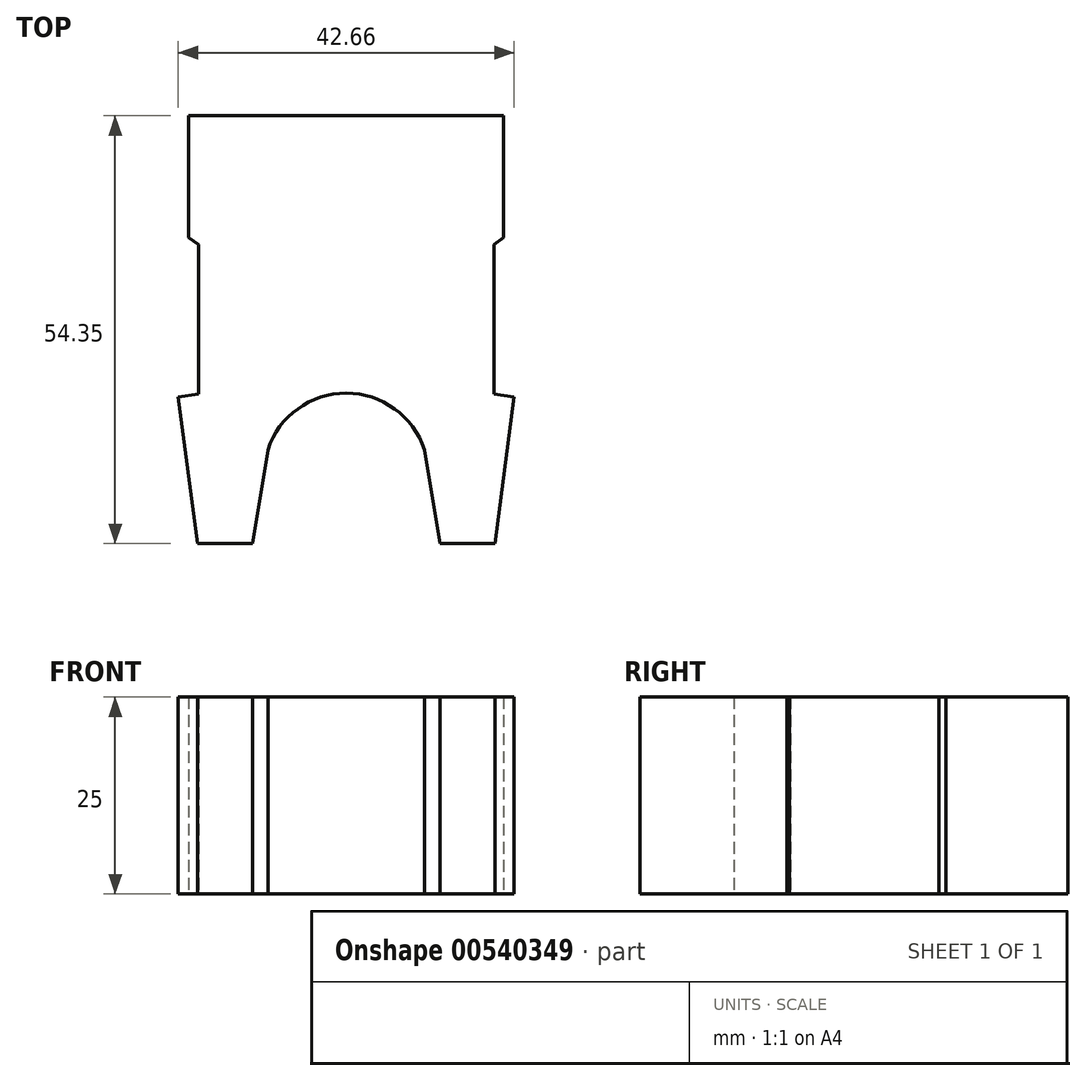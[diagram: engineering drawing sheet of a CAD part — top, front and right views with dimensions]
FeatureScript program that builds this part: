
annotation { "Feature Type Name" : "Feature", "Feature Type Description" : "" }
export const myFeature = defineFeature(function(context is Context, id is Id, definition is map)
    precondition{}
    {
        {
            var Q0;
            Q0=qCreatedBy(makeId("Top.planeOp"),FACE);
            var sketch = newSketch(context, id + "F0", { "sketchPlane" : qUnion([Q0])});
            skLineSegment(sketch, "E0", {"start": v(-21.33, -10.55) * mm, "end": v(-18.9, -29.2) * mm});
            skLineSegment(sketch, "E1", {"start": v(-21.33, -10.55) * mm, "end": v(-18.75, -10.21) * mm});
            skLineSegment(sketch, "E2", {"start": v(-18.75, -10.21) * mm, "end": v(-18.75, 8.79) * mm});
            skLineSegment(sketch, "E3", {"start": v(-18.75, 8.79) * mm, "end": v(-20, 9.66) * mm});
            skLineSegment(sketch, "E4", {"start": v(-20, 9.66) * mm, "end": v(-20, 25.16) * mm});
            skLineSegment(sketch, "E5", {"start": v(-20, 25.16) * mm, "end": v(0, 25.16) * mm});
            skLineSegment(sketch, "E6.MirrorCS", {"start": v(21.33, -10.55) * mm, "end": v(18.75, -10.21) * mm});
            skLineSegment(sketch, "E7.MirrorCS", {"start": v(18.75, 8.79) * mm, "end": v(20, 9.66) * mm});
            skLineSegment(sketch, "E8.MirrorCS", {"start": v(18.75, -10.21) * mm, "end": v(18.75, 8.79) * mm});
            skLineSegment(sketch, "E9.MirrorCS", {"start": v(20, 25.16) * mm, "end": v(0, 25.16) * mm});
            skLineSegment(sketch, "E10.MirrorCS", {"start": v(21.33, -10.55) * mm, "end": v(18.9, -29.2) * mm});
            skLineSegment(sketch, "E11.MirrorCS", {"start": v(20, 9.66) * mm, "end": v(20, 25.16) * mm});
            skLineSegment(sketch, "E12", {"start": v(-18.9, -29.2) * mm, "end": v(-11.9, -29.2) * mm});
            skLineSegment(sketch, "E13", {"start": v(18.9, -29.2) * mm, "end": v(11.9, -29.2) * mm});
            skLineSegment(sketch, "E14", {"start": v(-18.9, -29.2) * mm, "end": v(-20.45, -17.3) * mm});
            skLineSegment(sketch, "E15", {"start": v(18.9, -29.2) * mm, "end": v(20.45, -17.3) * mm});
            skLineSegment(sketch, "E16", {"start": v(-9.95, -17.3) * mm, "end": v(-11.9, -29.2) * mm});
            skLineSegment(sketch, "E17", {"start": v(9.95, -17.3) * mm, "end": v(11.9, -29.2) * mm});
            skArc(sketch, "E18", {"start": v(9.95, -17.3) * mm, "mid": v(0, -10.1) * mm, "end": v(-9.95, -17.3) * mm});
            skSolve(sketch);
        }
        {
            var Q0;
            Q0=makeQuery(id+"F0.imprint","IMPRINT",FACE,{"disambiguationData":[TD([[makeQuery(id+"F0.imprint","IMPRINT",EDGE,{"derivedFrom":sQuery(id+"F0.wireOp",EDGE,"E0")}),1.0]])]});
            extrude(context, id + "F1", {"entities" : qUnion([Q0]), "depth" : 25 * mm, "offsetDistance" : 25 * mm});
        }
    });
